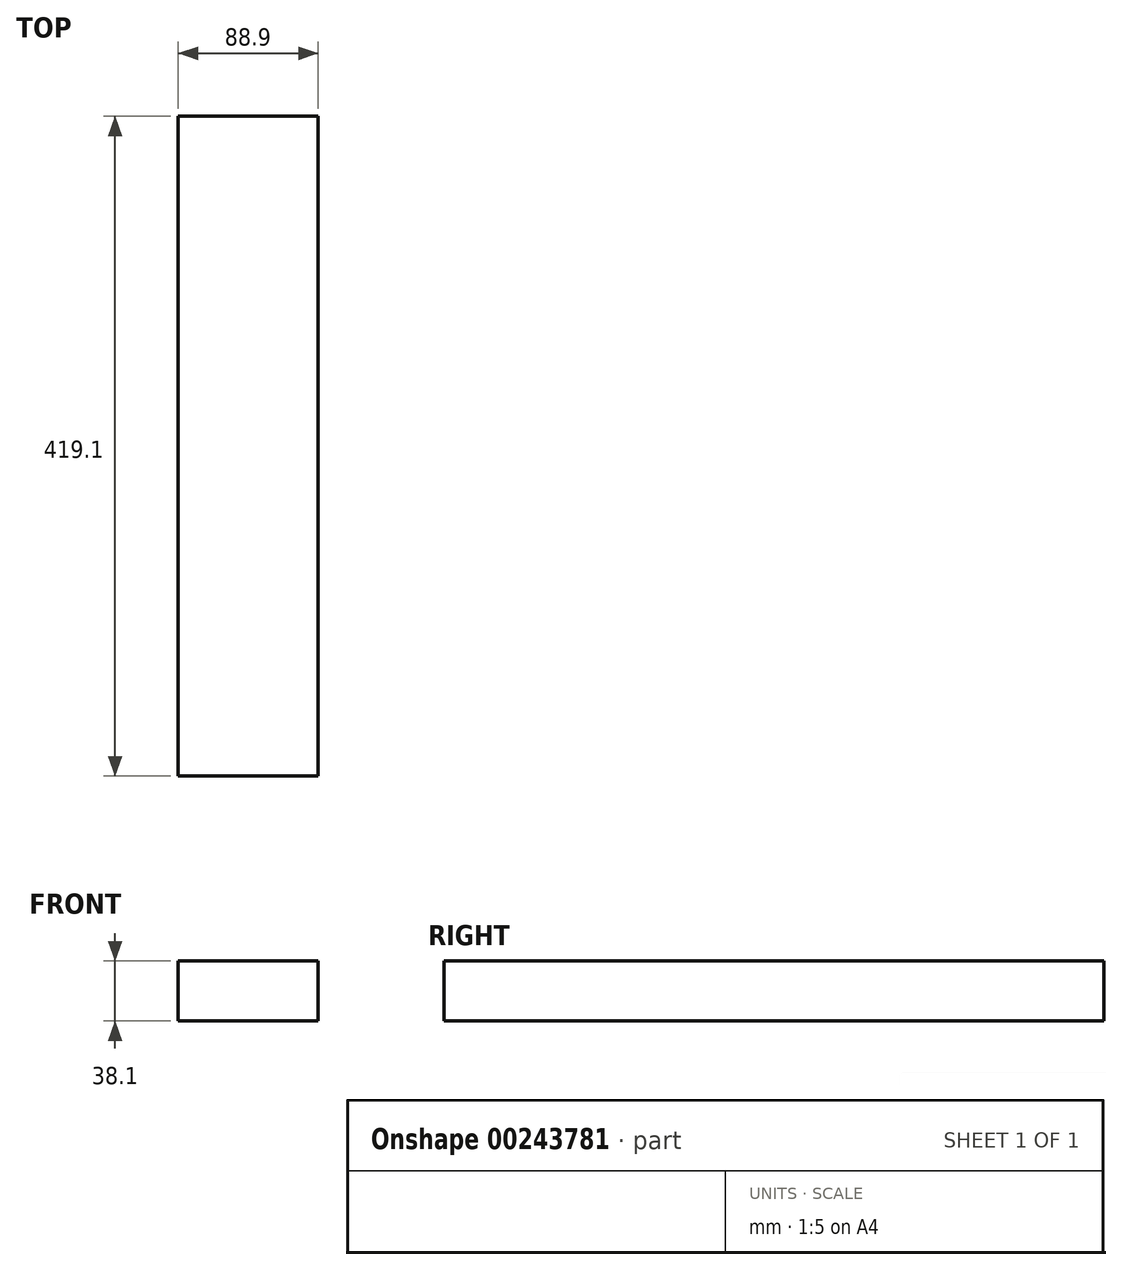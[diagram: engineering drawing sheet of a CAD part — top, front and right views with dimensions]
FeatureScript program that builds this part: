
annotation { "Feature Type Name" : "Feature", "Feature Type Description" : "" }
export const myFeature = defineFeature(function(context is Context, id is Id, definition is map)
    precondition{}
    {
        {
            var Q0;
            Q0=qCreatedBy(makeId("Front.planeOp"),FACE);
            var sketch = newSketch(context, id + "F0", { "sketchPlane" : qUnion([Q0])});
            skLineSegment(sketch, "E0.bottom", {"start": v(-59.53, 18.73) * mm, "end": v(29.37, 18.73) * mm});
            skLineSegment(sketch, "E0.top", {"start": v(-59.53, -19.37) * mm, "end": v(29.37, -19.37) * mm});
            skLineSegment(sketch, "E0.left", {"start": v(-59.53, 18.73) * mm, "end": v(-59.53, -19.37) * mm});
            skLineSegment(sketch, "E0.right", {"start": v(29.37, 18.73) * mm, "end": v(29.37, -19.37) * mm});
            skSolve(sketch);
        }
        {
            var Q0;
            Q0=makeQuery(id+"F0.imprint","IMPRINT",FACE,{"disambiguationData":[TD([[makeQuery(id+"F0.imprint","IMPRINT",EDGE,{"derivedFrom":sQuery(id+"F0.wireOp",EDGE,"E0.bottom")}),-1.0]])]});
            extrude(context, id + "F1", {"entities" : qUnion([Q0]), "depth" : 419.1 * mm});
        }
    });
